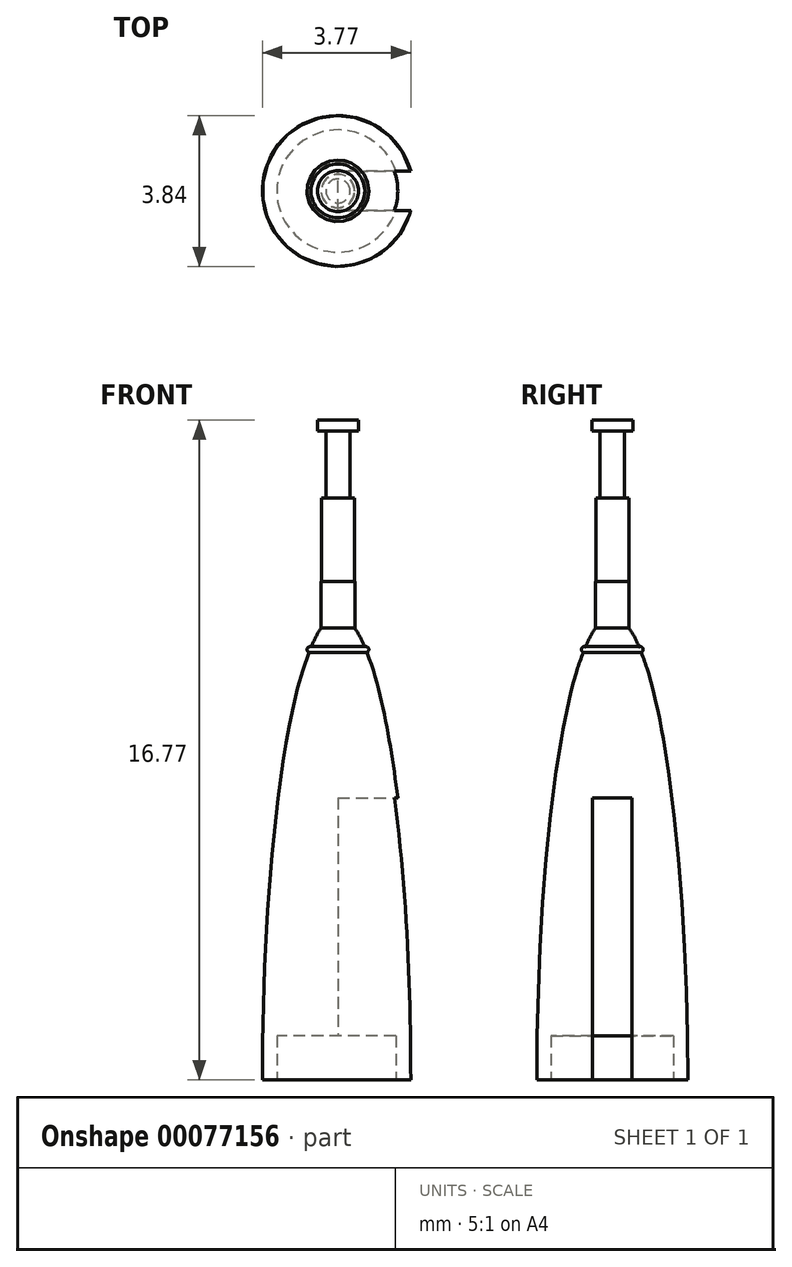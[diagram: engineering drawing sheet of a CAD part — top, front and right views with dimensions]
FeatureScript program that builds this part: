
annotation { "Feature Type Name" : "Feature", "Feature Type Description" : "" }
export const myFeature = defineFeature(function(context is Context, id is Id, definition is map)
    precondition{}
    {
        {
            var Q0;
            Q0=qCreatedBy(makeId("Front.planeOp"),FACE);
            var sketch = newSketch(context, id + "F0", { "sketchPlane" : qUnion([Q0])});
            skEllipticalArc(sketch, "E0", {});
            skLineSegment(sketch, "E1", {"start": v(0, 11.78) * mm, "end": v(0, -11.78) * mm});
            skLineSegment(sketch, "E2.bottom", {"start": v(-0.43, 11.48) * mm, "end": v(-0.43, 11.48) * mm});
            skLineSegment(sketch, "E2.top", {"start": v(-0.42, 12.66) * mm, "end": v(-0.43, 12.66) * mm});
            skLineSegment(sketch, "E2.left", {"start": v(0, 11.48) * mm, "end": v(0, 12.66) * mm});
            skLineSegment(sketch, "E2.right", {"start": v(-0.43, 11.48) * mm, "end": v(-0.43, 12.66) * mm});
            skLineSegment(sketch, "E3.left", {"start": v(0, 12.66) * mm, "end": v(0, 14.78) * mm});
            skLineSegment(sketch, "E3.right", {"start": v(-0.42, 12.66) * mm, "end": v(-0.42, 14.78) * mm});
            skLineSegment(sketch, "E4.left", {"start": v(0, 14.78) * mm, "end": v(0, 16.48) * mm});
            skLineSegment(sketch, "E4.right", {"start": v(-0.3, 14.78) * mm, "end": v(-0.3, 16.48) * mm});
            skLineSegment(sketch, "E5", {"start": v(-0.3, 14.78) * mm, "end": v(-0.42, 14.78) * mm});
            skArc(sketch, "E6", {"start": v(-0.68, 11) * mm, "mid": v(-0.78, 10.97) * mm, "end": v(-0.74, 10.87) * mm});
            skEllipticalArc(sketch, "E7.trimOffspring", {});
            skArc(sketch, "E8", {"start": v(-1, -10.01) * mm, "mid": v(-1.06, -10.1) * mm, "end": v(-0.97, -10.16) * mm});
            skEllipticalArc(sketch, "E9.trimOffspring", {});
            skLineSegment(sketch, "E10.bottom", {"start": v(-0.3, 16.48) * mm, "end": v(-0.52, 16.48) * mm});
            skLineSegment(sketch, "E10.top", {"start": v(0, 16.77) * mm, "end": v(-0.52, 16.77) * mm});
            skLineSegment(sketch, "E10.left", {"start": v(0, 16.48) * mm, "end": v(0, 16.77) * mm});
            skLineSegment(sketch, "E10.right", {"start": v(-0.52, 16.48) * mm, "end": v(-0.52, 16.77) * mm});
            const initialGuessF0  = {"E0": [0, 0, 0, 1, 0.011777514631263973, 0.001916683178784572, 0.22421039553335678, 0.36366982071250753], "E7.trimOffspring": [0, 0, 0, 1, 0.011777514631263973, 0.001916683178784572, 0.3950853549318617, 2.587374773479048], "E9.trimOffspring": [0, 0, 0, 1, 0.011777514631263973, 0.001916683178784572, 2.6108752879956154, 3.141592653589793]};
            skSetInitialGuess(sketch, initialGuessF0);
            skSolve(sketch);
        }
        {
            var Q0;
            Q0=makeQuery(id+"F0.imprint","IMPRINT",FACE,{"disambiguationData":[TD([[makeQuery(id+"F0.imprint","IMPRINT",EDGE,{"derivedFrom":sQuery(id+"F0.wireOp",EDGE,"E0")}),1.0]])]});
            var Q1;
            Q1=sQuery(id+"F0.wireOp",EDGE,"E1");
            revolve(context, id + "F1", {"entities" : qUnion([Q0]), "axis" : qUnion([Q1]), "revolveType" : RevolveType.FULL});
        }
        {
            var Q0;
            Q0=qCreatedBy(makeId("Front.planeOp"),FACE);
            var sketch = newSketch(context, id + "F2", { "sketchPlane" : qUnion([Q0])});
            skLineSegment(sketch, "E11.top", {"start": v(0, 1.13) * mm, "end": v(-1.55, 1.13) * mm});
            skLineSegment(sketch, "E11.left", {"start": v(0, 0) * mm, "end": v(0, 1.13) * mm});
            skLineSegment(sketch, "E11.right", {"start": v(-1.55, 0) * mm, "end": v(-1.55, 1.13) * mm});
            skLineSegment(sketch, "E12.MirrorCS", {"start": v(-1.55, 0) * mm, "end": v(-1.55, -1.13) * mm});
            skLineSegment(sketch, "E13.MirrorCS", {"start": v(0, -1.13) * mm, "end": v(-1.55, -1.13) * mm});
            skLineSegment(sketch, "E14.MirrorCS", {"start": v(0, 0) * mm, "end": v(0, -1.13) * mm});
            skSolve(sketch);
        }
        {
            var Q0;
            Q0=qSketchRegion(id+"F2",true);
            var Q1;
            Q1=sQuery(id+"F2.wireOp",EDGE,"E14.MirrorCS");
            revolve(context, id + "F3", {"operationType" : NewBodyOperationType.REMOVE, "entities" : qUnion([Q0]), "axis" : qUnion([Q1]), "revolveType" : RevolveType.FULL, "oppositeDirection" : true});
        }
        {
            var Q0;
            Q0=qCreatedBy(makeId("Front.planeOp"),FACE);
            var sketch = newSketch(context, id + "F4", { "sketchPlane" : qUnion([Q0])});
            skLineSegment(sketch, "E15.bottom", {"start": v(0, 7.17) * mm, "end": v(4.16, 7.17) * mm});
            skLineSegment(sketch, "E15.top", {"start": v(0, -6.88) * mm, "end": v(4.16, -6.88) * mm});
            skLineSegment(sketch, "E15.left", {"start": v(0, 7.17) * mm, "end": v(0, -6.88) * mm});
            skLineSegment(sketch, "E15.right", {"start": v(4.16, 7.17) * mm, "end": v(4.16, -6.88) * mm});
            skSolve(sketch);
        }
        {
            var Q0;
            Q0=makeQuery(id+"F4.imprint","IMPRINT",FACE,{"disambiguationData":[TD([[makeQuery(id+"F4.imprint","IMPRINT",EDGE,{"derivedFrom":sQuery(id+"F4.wireOp",EDGE,"E15.bottom")}),-1.0]])]});
            extrude(context, id + "F5", {"entities" : qUnion([Q0]), "operationType" : NewBodyOperationType.REMOVE, "depth" : 1 * mm, "offsetDistance" : 25 * mm, "symmetric" : true});
        }
        {
            var Q0;
            Q0=qCreatedBy(makeId("Front.planeOp"),FACE);
            var sketch = newSketch(context, id + "F6", { "sketchPlane" : qUnion([Q0])});
            skLineSegment(sketch, "E16.bottom", {"start": v(-7.38, 0) * mm, "end": v(7.87, 0) * mm});
            skLineSegment(sketch, "E16.top", {"start": v(-7.38, -13.03) * mm, "end": v(7.87, -13.03) * mm});
            skLineSegment(sketch, "E16.left", {"start": v(-7.38, 0) * mm, "end": v(-7.38, -13.03) * mm});
            skLineSegment(sketch, "E16.right", {"start": v(7.87, 0) * mm, "end": v(7.87, -13.03) * mm});
            skSolve(sketch);
        }
        {
            var Q0;
            Q0=makeQuery(id+"F6.imprint","IMPRINT",FACE,{"disambiguationData":[TD([[makeQuery(id+"F6.imprint","IMPRINT",EDGE,{"derivedFrom":sQuery(id+"F6.wireOp",EDGE,"E16.bottom")}),-1.0]])]});
            extrude(context, id + "F7", {"entities" : qUnion([Q0]), "operationType" : NewBodyOperationType.REMOVE, "depth" : 25 * mm, "offsetDistance" : 25 * mm, "symmetric" : true});
        }
    });
